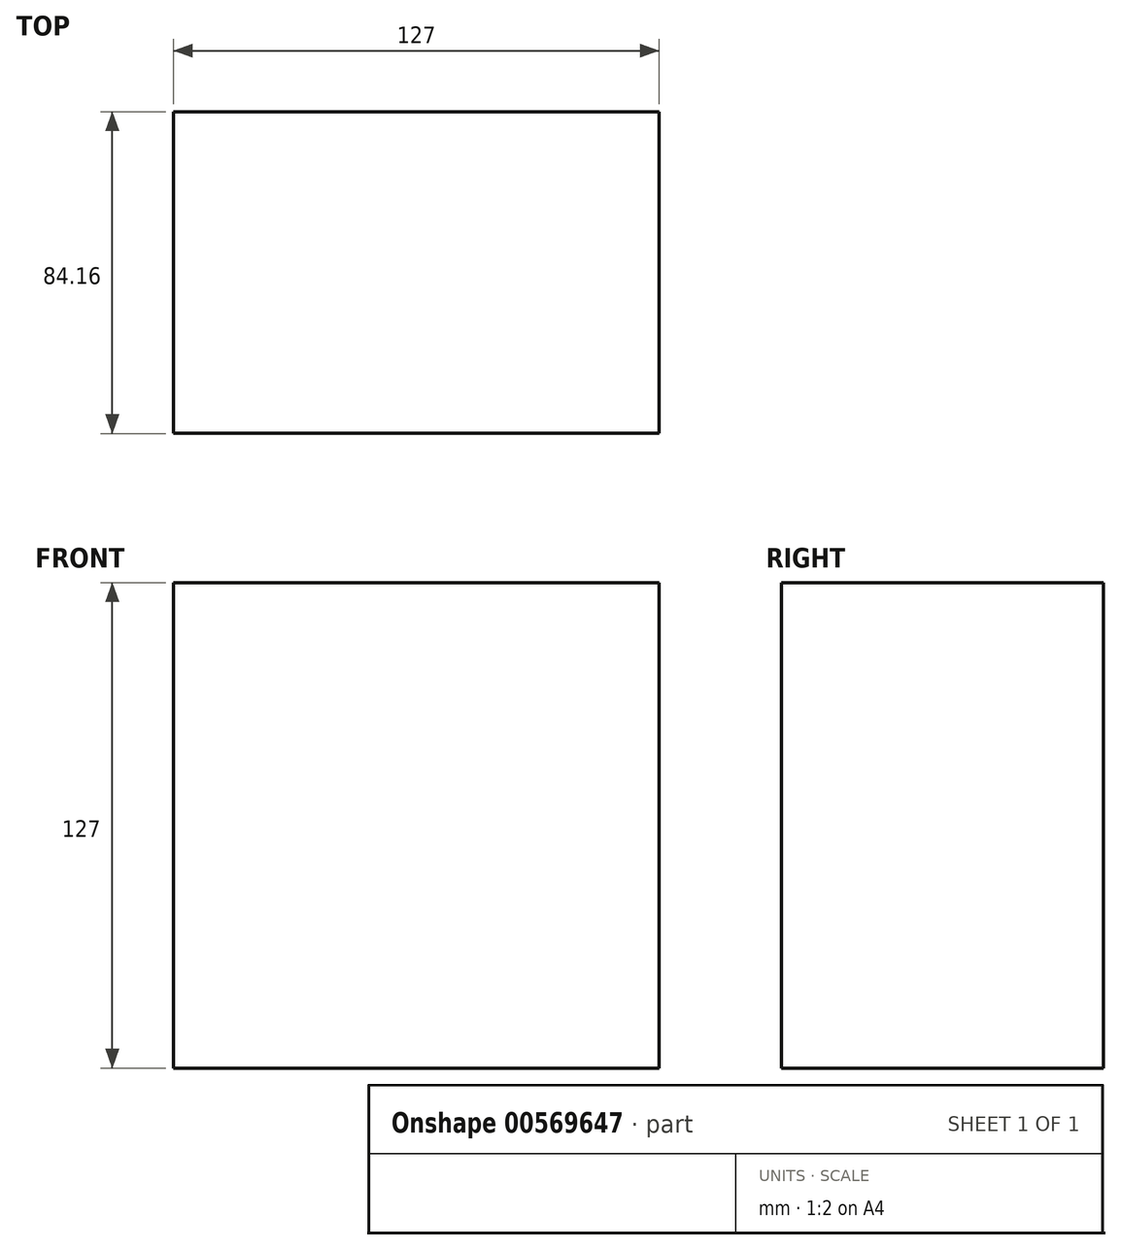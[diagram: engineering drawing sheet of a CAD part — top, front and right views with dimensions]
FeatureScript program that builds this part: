
annotation { "Feature Type Name" : "Feature", "Feature Type Description" : "" }
export const myFeature = defineFeature(function(context is Context, id is Id, definition is map)
    precondition{}
    {
        {
            var Q0;
            Q0=qCreatedBy(makeId("Front.planeOp"),FACE);
            var sketch = newSketch(context, id + "F0", { "sketchPlane" : qUnion([Q0])});
            skLineSegment(sketch, "E0.bottom", {"start": v(0, 0) * mm, "end": v(127, 0) * mm});
            skLineSegment(sketch, "E0.top", {"start": v(0, 127) * mm, "end": v(127, 127) * mm});
            skLineSegment(sketch, "E0.left", {"start": v(0, 0) * mm, "end": v(0, 127) * mm});
            skLineSegment(sketch, "E0.right", {"start": v(127, 0) * mm, "end": v(127, 127) * mm});
            skSolve(sketch);
        }
        {
            var Q0;
            Q0 = qSketchRegion(id + "F0", true);
            extrude(context, id + "F1", {"entities" : qUnion([Q0]), "depth" : 84.16 * mm, "offsetDistance" : 25.4 * mm});
        }
    });
